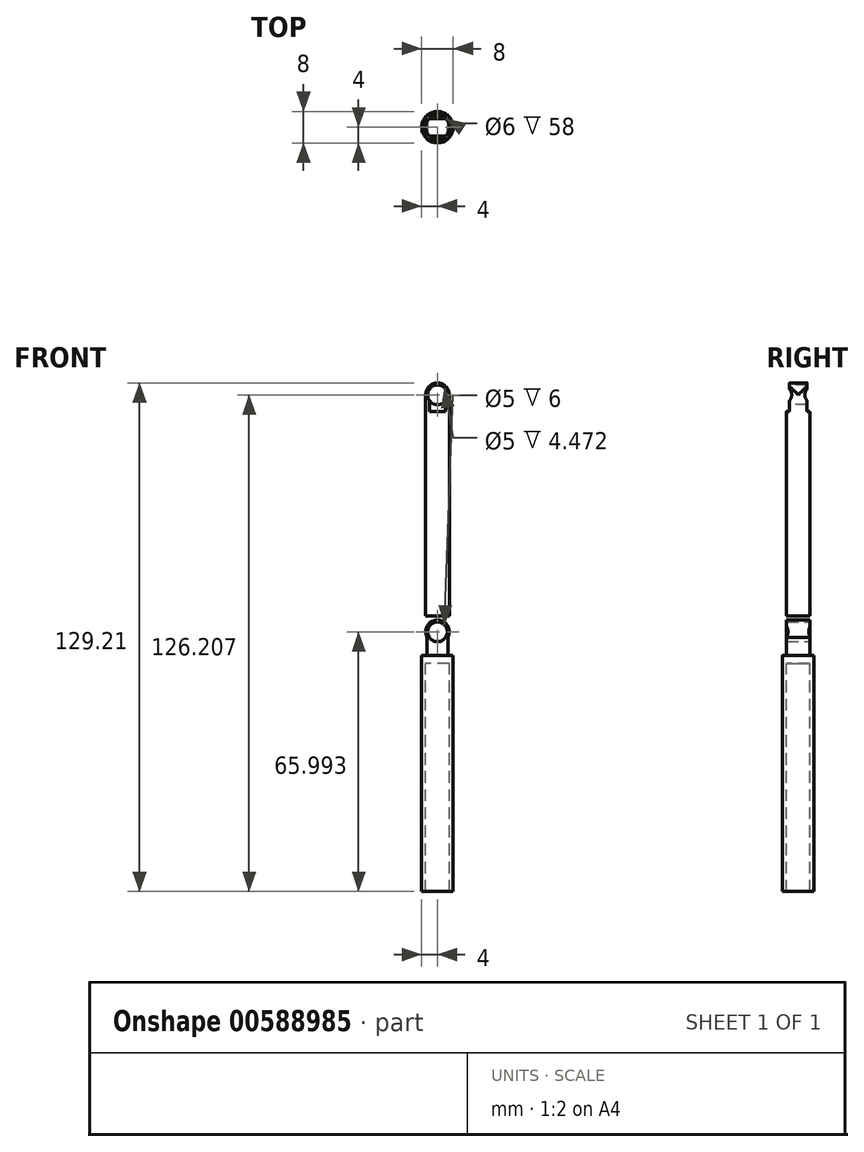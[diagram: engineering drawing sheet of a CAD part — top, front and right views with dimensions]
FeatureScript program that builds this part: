
annotation { "Feature Type Name" : "Feature", "Feature Type Description" : "" }
export const myFeature = defineFeature(function(context is Context, id is Id, definition is map)
    precondition{}
    {
        {
            var Q0;
            Q0=qCreatedBy(makeId("Top.planeOp"),FACE);
            var sketch = newSketch(context, id + "F0", { "sketchPlane" : qUnion([Q0])});
            skCircle(sketch, "E0", {"center": v(0, 0) * mm, "radius": 4 * mm});
            skCircle(sketch, "E1", {"center": v(0, 0) * mm, "radius": 3 * mm});
            skLineSegment(sketch, "E2", {"start": v(-2.65, 3) * mm, "end": v(2.65, 3) * mm});
            skLineSegment(sketch, "E3.MirrorCS", {"start": v(-2.65, -3) * mm, "end": v(2.65, -3) * mm});
            skSolve(sketch);
        }
        {
            var Q0;
            Q0 = qSketchRegion(id + "F0", true);
            var Q1;
            Q1=makeQuery(id+"F0.imprint","IMPRINT",FACE,{"disambiguationData":[TD([[makeQuery(id+"F0.imprint","IMPRINT",EDGE,{"derivedFrom":sQuery(id+"F0.wireOp",EDGE,"E0")}),1.0]])]});
            extrude(context, id + "F1", {"entities" : qUnion([Q0, Q1]), "oppositeDirection" : true, "depth" : 70 * mm, "offsetDistance" : 25 * mm});
        }
        {
            var Q0;
            Q0=makeQuery(id+"F0.imprint","IMPRINT",FACE,{"disambiguationData":[TD([[makeQuery(id+"F0.imprint","IMPRINT",EDGE,{"derivedFrom":sQuery(id+"F0.wireOp",EDGE,"E1")}),1.0]])]});
            extrude(context, id + "F2", {"entities" : qUnion([Q0]), "depth" : 60 * mm, "offsetDistance" : 25 * mm});
        }
        {
            var Q0;
            Q0=makeQuery(id+"F0.imprint","IMPRINT",FACE,{"disambiguationData":[TD([[makeQuery(id+"F0.imprint","IMPRINT",EDGE,{"derivedFrom":sQuery(id+"F0.wireOp",EDGE,"E1")}),1.0]])]});
            extrude(context, id + "F3", {"entities" : qUnion([Q0]), "operationType" : NewBodyOperationType.ADD, "oppositeDirection" : true, "depth" : 12 * mm, "offsetDistance" : 25 * mm});
        }
        {
            var Q0;
            {var subQ0=sQuery(id+"F0.wireOp",EDGE,"E2");var subQ1=sQuery(id+"F0.wireOp",EDGE,"E0");var subQ2=makeQuery(id+"F0.imprint","INTERSECT",VERTEX,{"disambiguationData":[OD(0.0)],"derivedFrom":[subQ1,subQ0]});Q0=makeQuery(id+"F0.imprint","IMPRINT",FACE,{"disambiguationData":[TD([[makeQuery(id+"F0.imprint","IMPRINT",EDGE,{"disambiguationData":[TD([[subQ2,1.0]])],"derivedFrom":subQ1}),1.0]])]});}
            var Q1;
            {var subQ0=sQuery(id+"F0.wireOp",EDGE,"E3.MirrorCS");var subQ1=sQuery(id+"F0.wireOp",EDGE,"E0");var subQ2=makeQuery(id+"F0.imprint","INTERSECT",VERTEX,{"disambiguationData":[OD(0.0)],"derivedFrom":[subQ1,subQ0]});Q1=makeQuery(id+"F0.imprint","IMPRINT",FACE,{"disambiguationData":[TD([[makeQuery(id+"F0.imprint","IMPRINT",EDGE,{"disambiguationData":[TD([[subQ2,-1.0]])],"derivedFrom":subQ1}),1.0]])]});}
            extrude(context, id + "F4", {"entities" : qUnion([Q0, Q1]), "operationType" : NewBodyOperationType.REMOVE, "oppositeDirection" : true, "depth" : 10 * mm, "offsetDistance" : 25 * mm});
        }
        {
            var Q0;
            Q0=makeQuery(id+"F4.boolean.opBoolean","COPY",FACE,{"derivedFrom":makeQuery(id+"F4.opExtrude","SWEPT_FACE",FACE,{"disambiguationData":[OSD([sQuery(id+"F0.wireOp",EDGE,"E2")])]})});
            var sketch = newSketch(context, id + "F5", { "sketchPlane" : qUnion([Q0])});
            skCircle(sketch, "E4", {"center": v(0, -4) * mm, "radius": 3 * mm});
            skPoint(sketch, "E4.centerSnap0", {"position": v(-2.65, -5) * mm});
            skCircle(sketch, "E5", {"center": v(0, -4) * mm, "radius": 2.5 * mm});
            skLineSegment(sketch, "E6.0.0", {"start": v(1.35, 0) * mm, "end": v(-1.35, 0) * mm});
            skLineSegment(sketch, "E6.0.1", {"start": v(-2.65, -4) * mm, "end": v(-2.65, -10) * mm});
            skLineSegment(sketch, "E6.0.2", {"start": v(-2.65, -10) * mm, "end": v(2.65, -10) * mm});
            skLineSegment(sketch, "E6.0.3", {"start": v(2.65, -10) * mm, "end": v(2.65, -4) * mm});
            skPoint(sketch, "E7.visualSharp", {"position": v(-2.65, 0) * mm});
            skPoint(sketch, "E8.visualSharp", {"position": v(2.65, 0) * mm});
            skLineSegment(sketch, "E9", {"start": v(4, 0) * mm, "end": v(4, -70) * mm});
            skLineSegment(sketch, "E10", {"start": v(-4, -70) * mm, "end": v(-4, 0) * mm});
            skLineSegment(sketch, "E11", {"start": v(-2.65, -10) * mm, "end": v(-4, -10) * mm});
            skLineSegment(sketch, "E12", {"start": v(2.65, -10) * mm, "end": v(4, -10) * mm});
            skLineSegment(sketch, "E13", {"start": v(-1.35, 0) * mm, "end": v(-4, 0) * mm});
            skLineSegment(sketch, "E14", {"start": v(1.35, 0) * mm, "end": v(4, 0) * mm});
            skSolve(sketch);
        }
        {
            var Q0;
            Q0=makeQuery(id+"F5.imprint","IMPRINT",FACE,{"disambiguationData":[TD([[makeQuery(id+"F5.imprint","IMPRINT",EDGE,{"derivedFrom":sQuery(id+"F5.wireOp",EDGE,"E5")}),1.0]])]});
            var Q1;
            {var subQ0=sQuery(id+"F5.wireOp",EDGE,"E11");Q1=makeQuery(id+"F5.imprint","IMPRINT",FACE,{"disambiguationData":[TD([[makeQuery(id+"F5.imprint","IMPRINT",EDGE,{"derivedFrom":subQ0}),-1.0]])]});}
            var Q2;
            {var subQ3=sQuery(id+"F5.wireOp",EDGE,"E12");Q2=makeQuery(id+"F5.imprint","IMPRINT",FACE,{"disambiguationData":[TD([[makeQuery(id+"F5.imprint","IMPRINT",EDGE,{"derivedFrom":subQ3}),1.0]])]});}
            var Q3;
            {var subQ5=sQuery(id+"F5.wireOp",EDGE,"E6.0.0");Q3=makeQuery(id+"F5.imprint","IMPRINT",FACE,{"disambiguationData":[TD([[makeQuery(id+"F5.imprint","IMPRINT",EDGE,{"derivedFrom":subQ5}),1.0]])]});}
            extrude(context, id + "F6", {"entities" : qUnion([Q0, Q1, Q2, Q3]), "operationType" : NewBodyOperationType.REMOVE, "oppositeDirection" : true, "depth" : 25 * mm, "offsetDistance" : 25 * mm});
        }
        {
            var Q0;
            Q0=makeQuery(id+"F2.opExtrude","CAP_FACE",FACE,{"disambiguationData":[OSD([sQuery(id+"F0.wireOp",EDGE,"E1")])],"isStart":false});
            var sketch = newSketch(context, id + "F7", { "sketchPlane" : qUnion([Q0])});
            skLineSegment(sketch, "E15", {"start": v(2, -2.24) * mm, "end": v(-2, -2.24) * mm});
            skLineSegment(sketch, "E16.MirrorCS", {"start": v(2, 2.24) * mm, "end": v(-2, 2.24) * mm});
            skSolve(sketch);
        }
        {
            var Q0;
            {var subQ0=sQuery(id+"F7.wireOp",EDGE,"E16.MirrorCS");Q0=makeQuery(id+"F7.imprint","IMPRINT",FACE,{"disambiguationData":[TD([[makeQuery(id+"F7.imprint","IMPRINT",EDGE,{"derivedFrom":subQ0}),-1.0]])]});}
            var Q1;
            {var subQ0=sQuery(id+"F7.wireOp",EDGE,"E15");Q1=makeQuery(id+"F7.imprint","IMPRINT",FACE,{"disambiguationData":[TD([[makeQuery(id+"F7.imprint","IMPRINT",EDGE,{"derivedFrom":subQ0}),1.0]])]});}
            extrude(context, id + "F8", {"entities" : qUnion([Q0, Q1]), "operationType" : NewBodyOperationType.REMOVE, "oppositeDirection" : true, "depth" : 8 * mm, "offsetDistance" : 25 * mm});
        }
        {
            var Q0;
            Q0=qCreatedBy(makeId("Front.planeOp"),FACE);
            var sketch = newSketch(context, id + "F9", { "sketchPlane" : qUnion([Q0])});
            skLineSegment(sketch, "E17", {"start": v(-3, 0) * mm, "end": v(-3, 60) * mm});
            skLineSegment(sketch, "E18", {"start": v(3, 60) * mm, "end": v(3, 0) * mm});
            skCircle(sketch, "E19", {"center": v(0, 56.2) * mm, "radius": 2.5 * mm});
            skCircle(sketch, "E20", {"center": v(0, 56.2) * mm, "radius": 3 * mm});
            skLineSegment(sketch, "E21", {"start": v(3, 60) * mm, "end": v(-3, 60) * mm});
            skSolve(sketch);
        }
        {
            var Q0;
            Q0=makeQuery(id+"F9.imprint","IMPRINT",FACE,{"disambiguationData":[TD([[makeQuery(id+"F9.imprint","IMPRINT",EDGE,{"derivedFrom":sQuery(id+"F9.wireOp",EDGE,"E19")}),1.0]])]});
            var Q1;
            {var subQ0=sQuery(id+"F9.wireOp",EDGE,"E21");Q1=makeQuery(id+"F9.imprint","IMPRINT",FACE,{"disambiguationData":[TD([[makeQuery(id+"F9.imprint","IMPRINT",EDGE,{"derivedFrom":subQ0}),1.0]])]});}
            extrude(context, id + "F10", {"entities" : qUnion([Q0, Q1]), "operationType" : NewBodyOperationType.REMOVE, "endBound" : BoundingType.SYMMETRIC, "oppositeDirection" : true, "depth" : 25 * mm, "offsetDistance" : 25 * mm});
        }
    });
